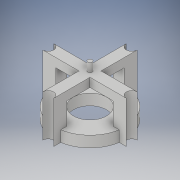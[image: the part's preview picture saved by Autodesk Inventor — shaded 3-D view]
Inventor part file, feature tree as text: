
AUTODESK INVENTOR PART (.ipt)
format: ipt  version: 2019 (Build 230136000, 136)  size: 215,552 bytes
history: native  units: mm
features: extrude x5, sketch x5
ambient origin geometry x8: Origin, YZ Plane, XZ Plane, XY Plane, X Axis, Y Axis, Z Axis, Center Point
bodies: Body1 (feature_tree), Body2 (feature_tree), Body3 (feature_tree)
feature tree (10):
  extrude  "Extrusion10"  Depth=32.0mm
  extrude  "Extrusion11"  Depth=2.5mm
  extrude  "Extrusion12"  Depth=2.5mm
  extrude  "Extrusion13"  Depth=16.0mm
  extrude  "Extrusion14"  Depth=16.0mm
  sketch  "Sketch9"  dims[d4=30.0mm d48=32.0mm]
  sketch  "Sketch10"  dims[d49=2.5mm d50=2.5mm]
  sketch  "Sketch11"  dims[d51=2.5mm d52=2.5mm]
  sketch  "Sketch12"  dims[d53=16.0mm d54=16.0mm]
  sketch  "Sketch13"  dims[d55=16.0mm d56=16.0mm d59=15.0mm d60=5.0mm d61=0.0mm d62=17.0mm d63=30.0mm d64=1.0mm d65=0.0mm d66=10.0mm d67=0.0mm d68=5.0mm d70=0.0mm d71=21.5mm d72=4.0mm d73=0.0mm d74=2.0mm d75=4.0mm d76=0.0mm]
